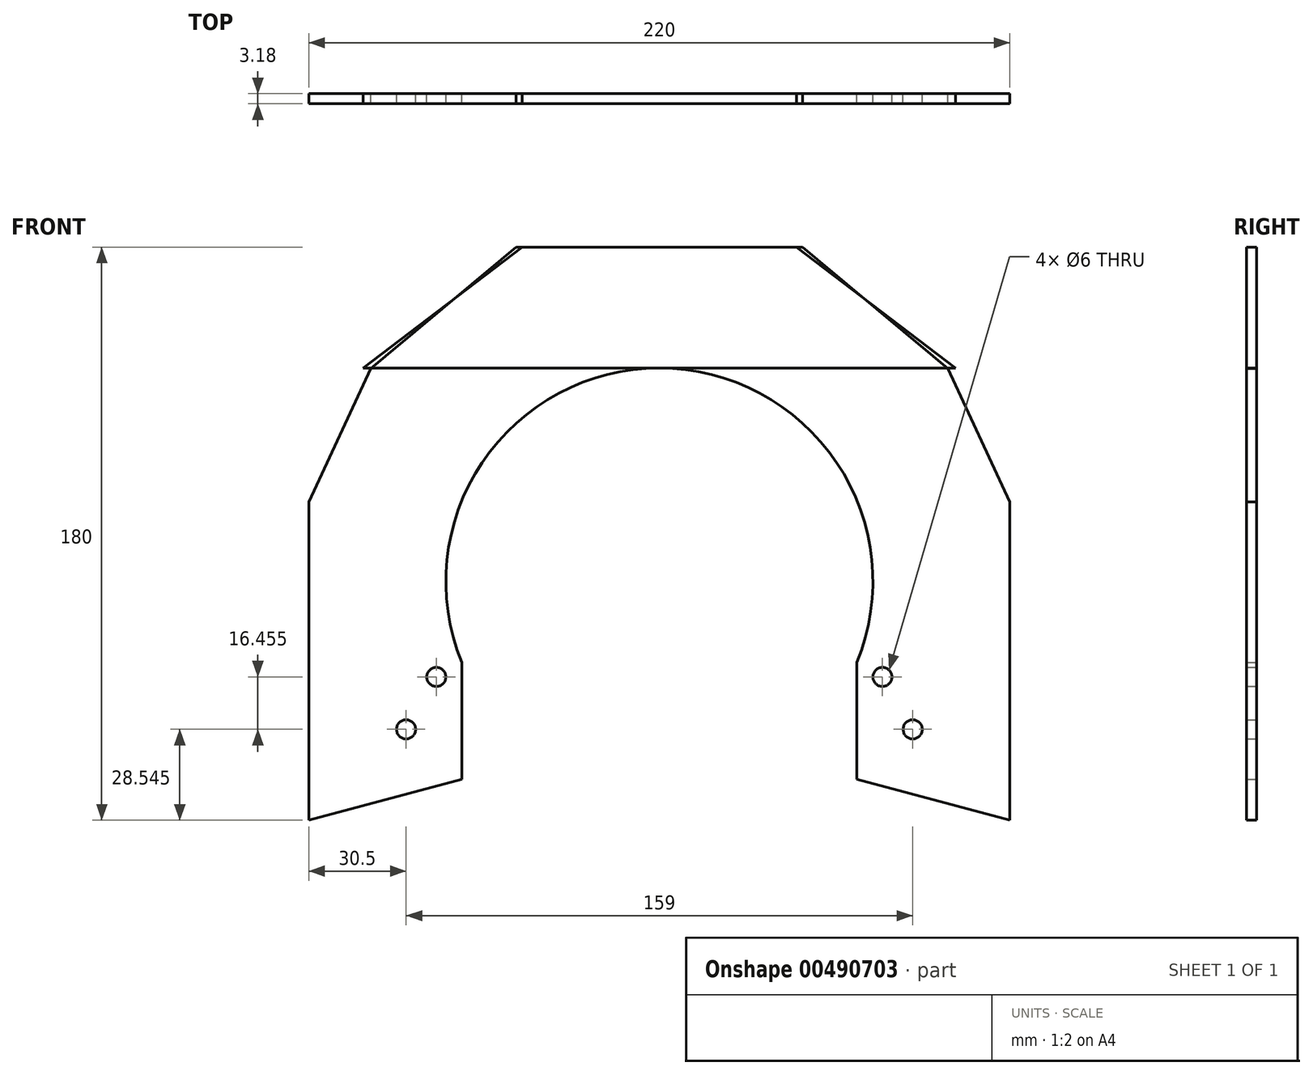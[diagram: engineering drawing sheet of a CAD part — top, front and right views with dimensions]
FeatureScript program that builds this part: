
annotation { "Feature Type Name" : "Feature", "Feature Type Description" : "" }
export const myFeature = defineFeature(function(context is Context, id is Id, definition is map)
    precondition{}
    {
        {
            var Q0;
            Q0=qCreatedBy(makeId("Front.planeOp"),FACE);
            var sketch = newSketch(context, id + "F0", { "sketchPlane" : qUnion([Q0])});
            skLineSegment(sketch, "E0.bottom", {"start": v(-110, 105) * mm, "end": v(93, 105) * mm, "construction": true});
            skLineSegment(sketch, "E0.top", {"start": v(-110, -75) * mm, "end": v(93, -75) * mm, "construction": true});
            skLineSegment(sketch, "E0.left", {"start": v(-110, 105) * mm, "end": v(-110, -75) * mm, "construction": true});
            skLineSegment(sketch, "E0.right", {"start": v(93, 105) * mm, "end": v(93, -75) * mm, "construction": true});
            skLineSegment(sketch, "E1", {"start": v(0, 67) * mm, "end": v(93, 67) * mm});
            skLineSegment(sketch, "E2", {"start": v(-62, 105) * mm, "end": v(-62, -75) * mm, "construction": true});
            skPoint(sketch, "E3", {"position": v(-110, 25) * mm});
            skPoint(sketch, "E4", {"position": v(-45, 105) * mm});
            skPoint(sketch, "E5", {"position": v(43, 105) * mm});
            skLineSegment(sketch, "E6", {"start": v(93, 67) * mm, "end": v(43, 105) * mm});
            skLineSegment(sketch, "E7", {"start": v(-110, 25) * mm, "end": v(-90.5, 66.82) * mm});
            skLineSegment(sketch, "E8", {"start": v(-45, 105) * mm, "end": v(-90.5, 66.82) * mm});
            skLineSegment(sketch, "E9", {"start": v(-110, -75) * mm, "end": v(-62, -62.14) * mm});
            skLineSegment(sketch, "E10", {"start": v(-67, 27.28) * mm, "end": v(-67, -21.54) * mm, "construction": true});
            skPoint(sketch, "E11", {"position": v(-62, -25.4) * mm});
            skArc(sketch, "E12", {"start": v(0, 67) * mm, "mid": v(-55.64, 37.33) * mm, "end": v(-62, -25.4) * mm});
            skLineSegment(sketch, "E13", {"start": v(-45, 105) * mm, "end": v(43, 105) * mm});
            skLineSegment(sketch, "E14", {"start": v(-110, 25) * mm, "end": v(-110, -75) * mm});
            skLineSegment(sketch, "E15", {"start": v(-62, -25.4) * mm, "end": v(-62, -62.14) * mm});
            skLineSegment(sketch, "E16", {"start": v(-98.87, -70) * mm, "end": v(-69.7, -19.48) * mm, "construction": true});
            skLineSegment(sketch, "E17", {"start": v(-90.2, -75) * mm, "end": v(-55.16, -14.3) * mm, "construction": true});
            skLineSegment(sketch, "E18", {"start": v(-90.2, -75) * mm, "end": v(-98.87, -70) * mm, "construction": true});
            skLineSegment(sketch, "E19", {"start": v(-63.17, -28.17) * mm, "end": v(-80.67, -58.48) * mm});
            skLineSegment(sketch, "E20", {"start": v(-63.17, -28.17) * mm, "end": v(-68.37, -25.17) * mm});
            skLineSegment(sketch, "E21", {"start": v(-68.37, -25.17) * mm, "end": v(-72.98, -25.17) * mm});
            skLineSegment(sketch, "E22", {"start": v(-72.98, -25.17) * mm, "end": v(-84.83, -45.69) * mm});
            skCircle(sketch, "E23", {"center": v(-79.5, -46.45) * mm, "radius": 3 * mm});
            skCircle(sketch, "E24", {"center": v(-70, -30) * mm, "radius": 3 * mm});
            skLineSegment(sketch, "E25", {"start": v(-70, -30) * mm, "end": v(-79.5, -46.45) * mm, "construction": true});
            skCircle(sketch, "E26", {"center": v(-79.5, -46.45) * mm, "radius": 2.5 * mm});
            skCircle(sketch, "E27", {"center": v(-70, -30) * mm, "radius": 2.5 * mm});
            skLineSegment(sketch, "E28", {"start": v(-84.46, -47.07) * mm, "end": v(-72.18, -43.78) * mm});
            skLineSegment(sketch, "E29", {"start": v(-80.67, -58.48) * mm, "end": v(-81.54, -57.98) * mm});
            skLineSegment(sketch, "E30", {"start": v(-81.54, -57.98) * mm, "end": v(-84.83, -45.69) * mm});
            skSolve(sketch);
        }
        {
            var Q0;
            Q0=makeQuery(id+"F0.imprint","IMPRINT",FACE,{"disambiguationData":[TD([[makeQuery(id+"F0.imprint","IMPRINT",EDGE,{"derivedFrom":sQuery(id+"F0.wireOp",EDGE,"E1")}),1.0]])]});
            var Q1;
            Q1=makeQuery(id+"F0.imprint","IMPRINT",FACE,{"disambiguationData":[TD([[makeQuery(id+"F0.imprint","IMPRINT",EDGE,{"derivedFrom":sQuery(id+"F0.wireOp",EDGE,"E19")}),-1.0]])]});
            var Q2;
            {var subQ0=sQuery(id+"F0.wireOp",EDGE,"E20");Q2=makeQuery(id+"F0.imprint","IMPRINT",FACE,{"disambiguationData":[TD([[makeQuery(id+"F0.imprint","IMPRINT",EDGE,{"derivedFrom":subQ0}),1.0]])]});}
            extrude(context, id + "F1", {"entities" : qUnion([Q0, Q1, Q2]), "depth" : 3.17 * mm});
        }
        {
            var Q0;
            Q0=makeQuery(id+"F1.opExtrude","SWEPT_BODY",BODY,{"disambiguationData":[OSD([sQuery(id+"F0.wireOp",EDGE,"E1"),sQuery(id+"F0.wireOp",EDGE,"E6"),sQuery(id+"F0.wireOp",EDGE,"E7"),sQuery(id+"F0.wireOp",EDGE,"E8"),sQuery(id+"F0.wireOp",EDGE,"E9"),sQuery(id+"F0.wireOp",EDGE,"E12"),sQuery(id+"F0.wireOp",EDGE,"E13"),sQuery(id+"F0.wireOp",EDGE,"E14"),sQuery(id+"F0.wireOp",EDGE,"E15"),sQuery(id+"F0.wireOp",EDGE,"E23"),sQuery(id+"F0.wireOp",EDGE,"E24")])]});
            var Q1;
            Q1=qCreatedBy(makeId("Right.planeOp"),FACE);
            mirror(context, id + "F2", {"entities" : qUnion([Q0]), "mirrorPlane" : qUnion([Q1])});
        }
    });
